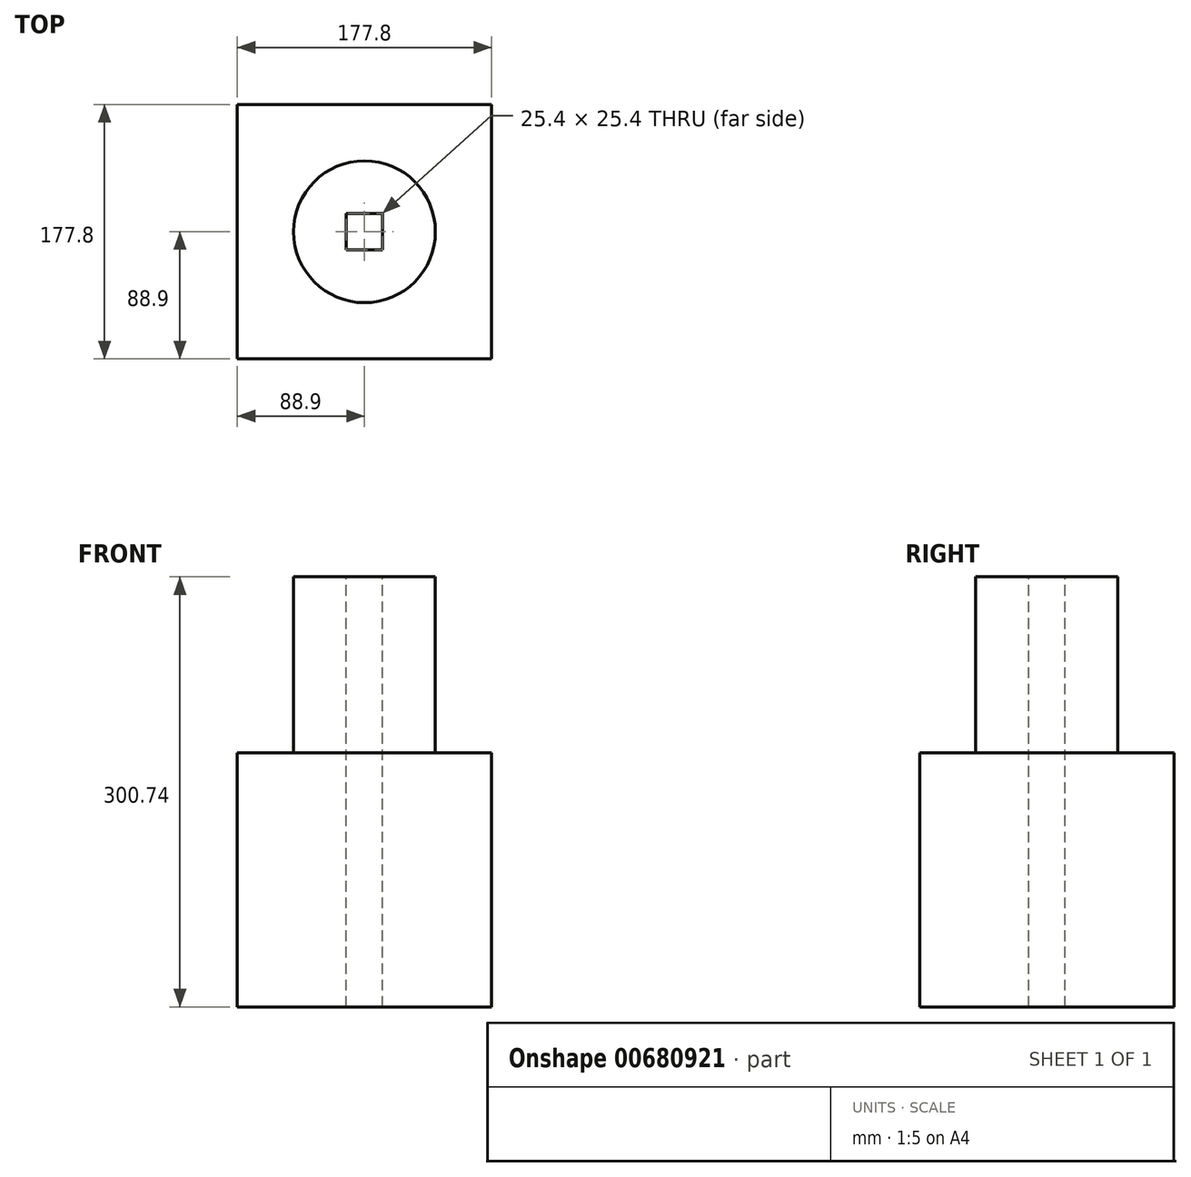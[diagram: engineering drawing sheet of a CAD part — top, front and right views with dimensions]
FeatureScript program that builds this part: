
annotation { "Feature Type Name" : "Feature", "Feature Type Description" : "" }
export const myFeature = defineFeature(function(context is Context, id is Id, definition is map)
    precondition{}
    {
        {
            var Q0;
            Q0=qCreatedBy(makeId("Top.planeOp"),FACE);
            var sketch = newSketch(context, id + "F0", { "sketchPlane" : qUnion([Q0])});
            skCircle(sketch, "E0", {"center": v(0, 0) * mm, "radius": 49.62 * mm});
            skSolve(sketch);
        }
        {
            var Q0;
            Q0=makeQuery(id+"F0.imprint","IMPRINT",FACE,{"disambiguationData":[TD([[makeQuery(id+"F0.imprint","IMPRINT",EDGE,{"derivedFrom":sQuery(id+"F0.wireOp",EDGE,"E0")}),1.0]])]});
            extrude(context, id + "F1", {"entities" : qUnion([Q0]), "depth" : 122.94 * mm, "offsetDistance" : 25.4 * mm});
        }
        {
            var Q0;
            Q0=qCreatedBy(makeId("Top.planeOp"),FACE);
            var sketch = newSketch(context, id + "F2", { "sketchPlane" : qUnion([Q0])});
            skLineSegment(sketch, "E1.bottom", {"start": v(88.9, -88.9) * mm, "end": v(-88.9, -88.9) * mm});
            skLineSegment(sketch, "E1.top", {"start": v(88.9, 88.9) * mm, "end": v(-88.9, 88.9) * mm});
            skLineSegment(sketch, "E1.left", {"start": v(88.9, -88.9) * mm, "end": v(88.9, 88.9) * mm});
            skLineSegment(sketch, "E1.right", {"start": v(-88.9, -88.9) * mm, "end": v(-88.9, 88.9) * mm});
            skPoint(sketch, "E1.middle", {"position": v(0, 0) * mm});
            skSolve(sketch);
        }
        {
            var Q0;
            Q0 = qSketchRegion(id + "F2", true);
            extrude(context, id + "F3", {"entities" : qUnion([Q0]), "operationType" : NewBodyOperationType.ADD, "oppositeDirection" : true, "depth" : 177.8 * mm, "offsetDistance" : 25.4 * mm});
        }
        {
            var Q0;
            Q0=makeQuery(id+"F1.opExtrude","CAP_FACE",FACE,{"disambiguationData":[OSD([sQuery(id+"F0.wireOp",EDGE,"E0")])],"isStart":false});
            var sketch = newSketch(context, id + "F4", { "sketchPlane" : qUnion([Q0])});
            skLineSegment(sketch, "E2.bottom", {"start": v(-12.7, 12.7) * mm, "end": v(12.7, 12.7) * mm});
            skLineSegment(sketch, "E2.top", {"start": v(-12.7, -12.7) * mm, "end": v(12.7, -12.7) * mm});
            skLineSegment(sketch, "E2.left", {"start": v(-12.7, 12.7) * mm, "end": v(-12.7, -12.7) * mm});
            skLineSegment(sketch, "E2.right", {"start": v(12.7, 12.7) * mm, "end": v(12.7, -12.7) * mm});
            skPoint(sketch, "E2.middle", {"position": v(0, 0) * mm});
            skSolve(sketch);
        }
        {
            var Q0;
            Q0=makeQuery(id+"F4.imprint","IMPRINT",FACE,{"disambiguationData":[TD([[makeQuery(id+"F4.imprint","IMPRINT",EDGE,{"derivedFrom":sQuery(id+"F4.wireOp",EDGE,"E2.bottom")}),-1.0]])]});
            extrude(context, id + "F5", {"entities" : qUnion([Q0]), "operationType" : NewBodyOperationType.REMOVE, "oppositeDirection" : true, "depth" : 376.94 * mm, "offsetDistance" : 25.4 * mm});
        }
    });
